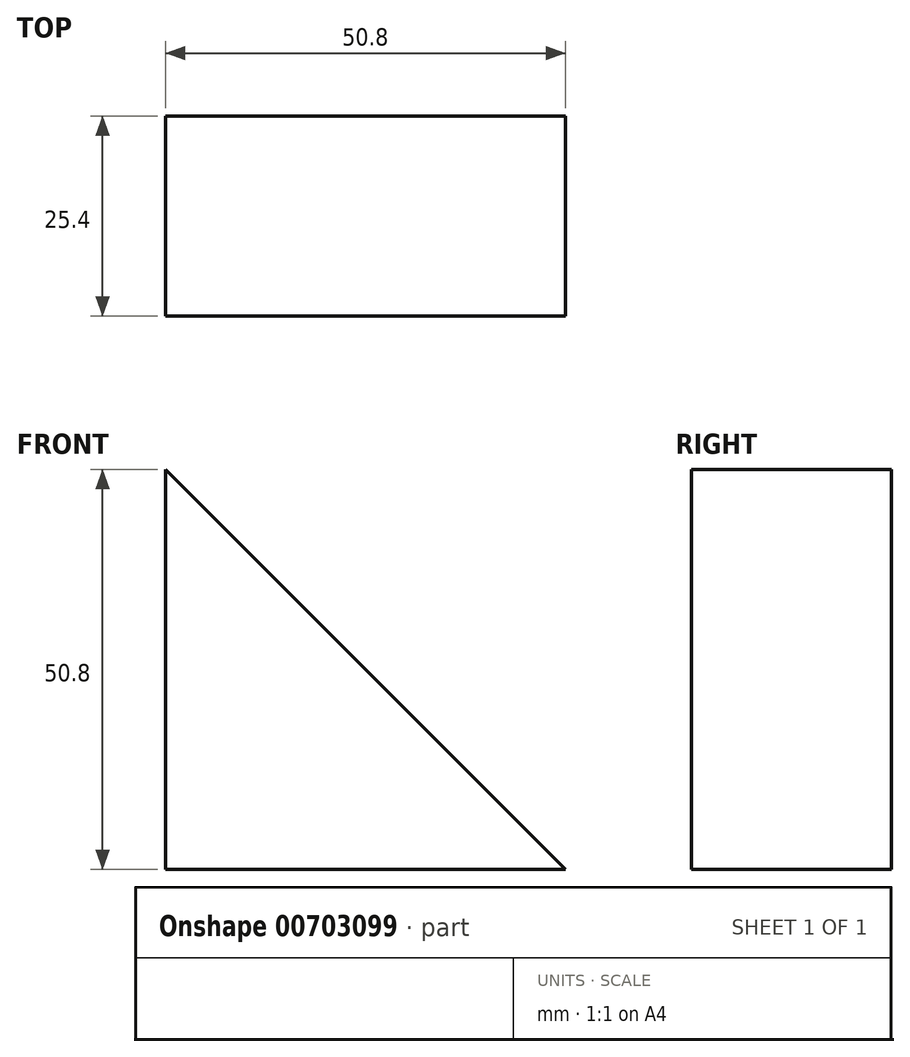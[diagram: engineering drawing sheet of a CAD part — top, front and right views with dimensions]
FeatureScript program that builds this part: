
annotation { "Feature Type Name" : "Feature", "Feature Type Description" : "" }
export const myFeature = defineFeature(function(context is Context, id is Id, definition is map)
    precondition{}
    {
        {
            var Q0;
            Q0=qCreatedBy(makeId("Front.planeOp"),FACE);
            var sketch = newSketch(context, id + "F0", { "sketchPlane" : qUnion([Q0])});
            skLineSegment(sketch, "E0", {"start": v(-26.64, 17.1) * mm, "end": v(-26.64, -33.7) * mm});
            skLineSegment(sketch, "E1", {"start": v(-26.64, -33.7) * mm, "end": v(24.16, -33.7) * mm});
            skLineSegment(sketch, "E2", {"start": v(-26.64, 17.1) * mm, "end": v(24.16, -33.7) * mm});
            skSolve(sketch);
        }
        {
            var Q0;
            Q0=makeQuery(id+"F0.imprint","IMPRINT",FACE,{"disambiguationData":[TD([[makeQuery(id+"F0.imprint","IMPRINT",EDGE,{"derivedFrom":sQuery(id+"F0.wireOp",EDGE,"E0")}),1.0]])]});
            extrude(context, id + "F1", {"entities" : qUnion([Q0]), "depth" : 25.4 * mm, "offsetDistance" : 25.4 * mm});
        }
    });
